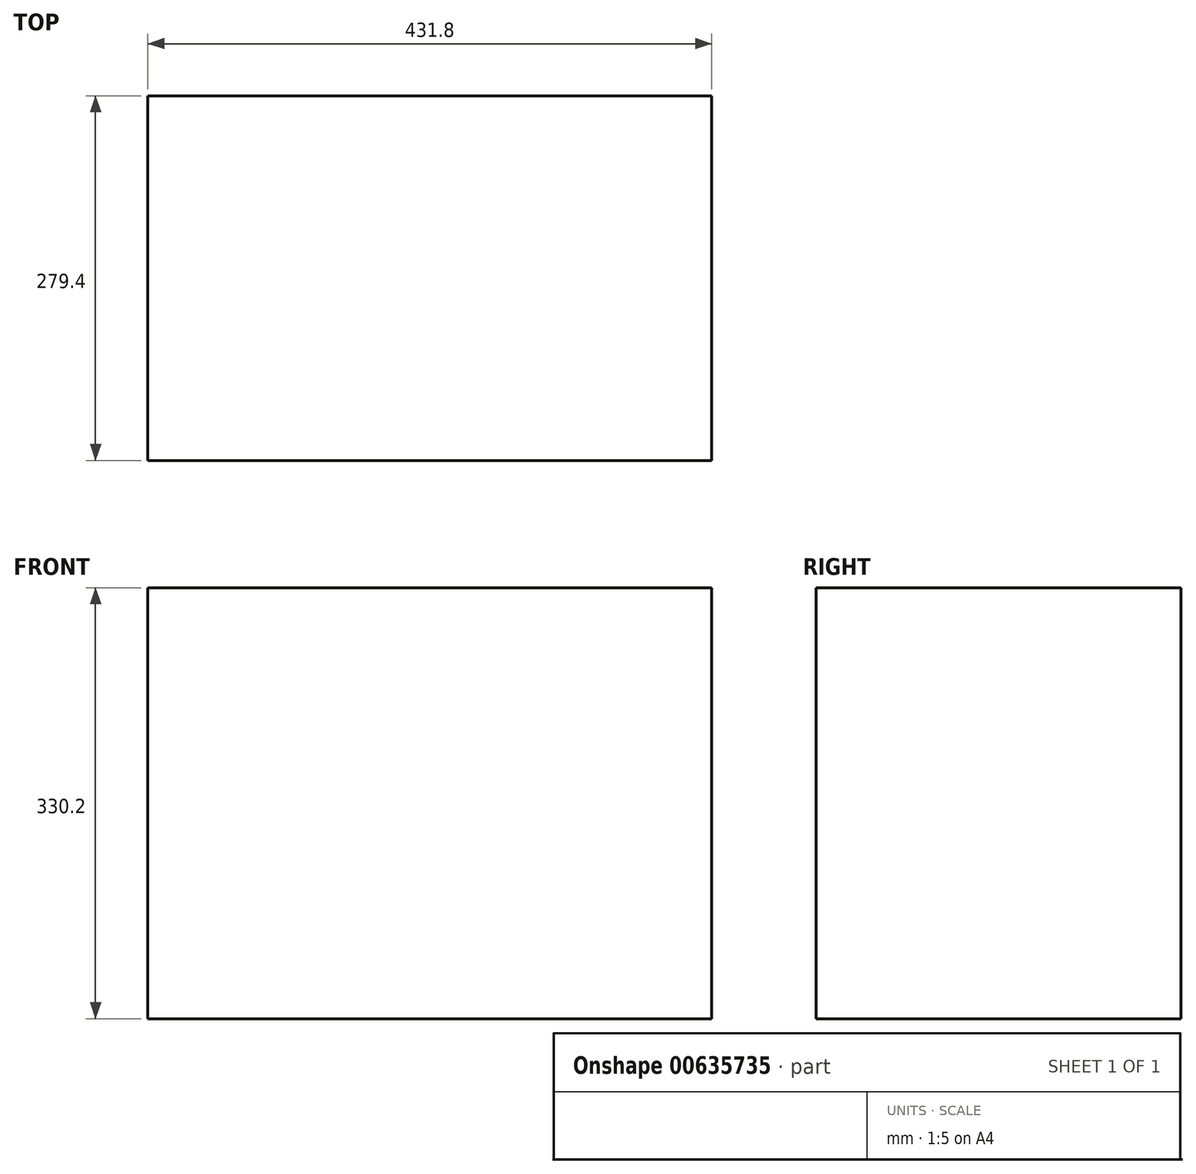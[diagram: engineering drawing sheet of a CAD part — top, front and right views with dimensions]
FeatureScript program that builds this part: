
annotation { "Feature Type Name" : "Feature", "Feature Type Description" : "" }
export const myFeature = defineFeature(function(context is Context, id is Id, definition is map)
    precondition{}
    {
        {
            var Q0;
            Q0=qCreatedBy(makeId("Front.planeOp"),FACE);
            var sketch = newSketch(context, id + "F0", { "sketchPlane" : qUnion([Q0])});
            skLineSegment(sketch, "E0.bottom", {"start": v(-332.97, 277.17) * mm, "end": v(98.83, 277.17) * mm});
            skLineSegment(sketch, "E0.top", {"start": v(-332.97, -53.03) * mm, "end": v(98.83, -53.03) * mm});
            skLineSegment(sketch, "E0.left", {"start": v(-332.97, 277.17) * mm, "end": v(-332.97, -53.03) * mm});
            skLineSegment(sketch, "E0.right", {"start": v(98.83, 277.17) * mm, "end": v(98.83, -53.03) * mm});
            skSolve(sketch);
        }
        {
            var Q0;
            Q0 = qSketchRegion(id + "F0", true);
            extrude(context, id + "F1", {"entities" : qUnion([Q0]), "depth" : 279.4 * mm, "offsetDistance" : 25.4 * mm});
        }
    });
